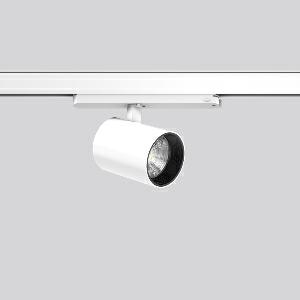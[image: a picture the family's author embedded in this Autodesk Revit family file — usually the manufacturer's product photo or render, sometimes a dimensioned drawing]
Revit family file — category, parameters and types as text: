
# Revit family: deecos_s_mini_track-in_742256_002_76_ecb4
name_source: partatom
category: Lighting Fixtures
units: mm (PartAtom-declared; Revit-internal decimal feet)

## family parameters
Cut with Voids When Loaded = No
Host = Face
Light Source = No
Part Type = Normal
Room Calculation Point = No
Round Connector Dimension = Use Diameter
Shared = No

## types (1)
- DEECOS S mini track-in (1 x LED Modul 930, 2250 lm, 3000)
    Apparent Load = 20 VA
    Approval mark = CE
    CIE Flux Codes = 80 99 100 100 100
    Color Rendering = 90
    Color Temperature = 3000
    Default Elevation = 1800 mm
    Description = Series: DEECOS S mini track-in
LED surface-mounted projector in modern design with no visible cooling ribs. Housing: die-cast aluminium, powder-coated. Rotation range: 356°. Swivel range: 90°. Black plastic ring and recessed LED to prevent glare from the side. Optical assembly with lens made of plastic (polycarbonate) for the best homogeneous light distribution - can be changed without tools. Best colour rendering index Ra>90. With adapter for RZB 3-circuit DALI tracks. Suitable for Track on ceiling, Wall track. Track-in driver integrated into the adapter. High quality converter without flickering and stroboscopic effect. The following accessories can be mounted without use of tools: interchangeable lenses, decorative glasses, honeycomb louvre, clear and frosted diffusers, white interchangeable plastic ring. 
Colour: traffic white, matt (RAL 9016)
Diameter: 87 mm
Height: 135 mm
Lamp: LED
Socket: without socket
Colour temperature: 3000K
Colour rendering index (CRI): 92
System power: 20 W
Rated luminous flux: 2250 lm
Luminous efficiency: 113 lm/W
Control gear: Converter, dimmable, DALI
Protection class: II
Type of protection: IP 20
    Height = 135 mm
    Lamp = 1 x LED Modul 930
    Lamp Light Flux = 2250 lm
    Lamp count = 1
    Length = 87 mm
    Lifetime = 50000 h
    Luminous efficacy = 113 lm/W
    Manufacturer = RZB
    ModVariant = No
    Model = 742256.002.76
    Mounting Place = Ceiling
    Mounting Type = Rail mounted
    Number of Poles = 1
    OnlyDefault = Yes
    Power Factor = 1
    Product Name = DEECOS S mini track-in
    Product group = Track mounted projectors
    ProductGroupID = 301
    Protection Class = Protection class II
    Protection Degree = IP 20
    RLX_Detail_Level = 1
    RLX_Emergency_Light_Flux = 0 lm
    RLX_Emergency_Type = 0
    RLX_Emergency_Type_DB = No
    RlxData = <blob elided: 35393 chars, md5=c5602fff>
    Socket = socket
    Standby Power = 0 W
    System Light Flux = 2250 lm
    System Power = 20 W
    Type Comments = Product without accessories
    Type Image = 742108.002.jpg
    URL = http://relux.com
    VarID = ---
    Voltage = 230 V
    Voltage Range = 220-240 V
    Weight = 0.00 kg
    Width = 0 mm  [stored 0 ft]

note: [stored X ft] marks values corroborated as IEEE doubles in the binary element streams (Revit-internal decimal feet)

## geometry (parser evidence)
native form markers: Blend x4, Sweep x12
no freeform markers — native parametric forms only
